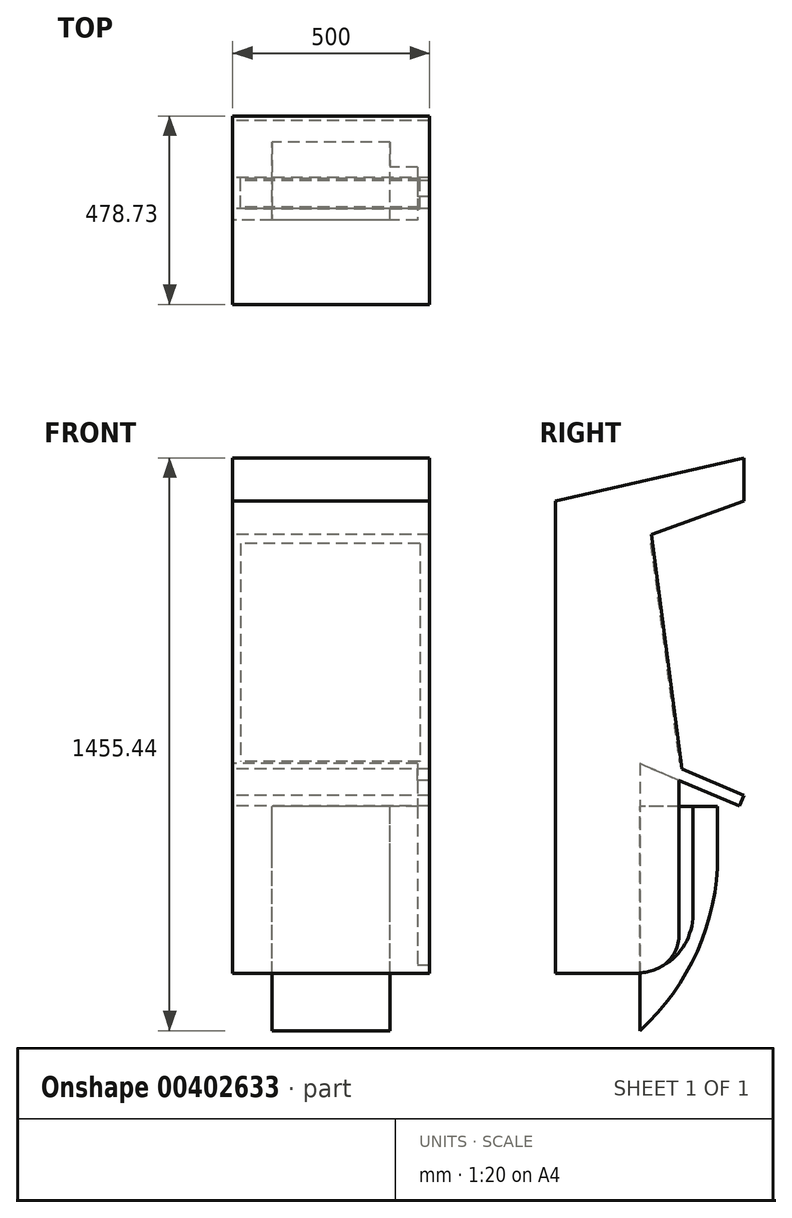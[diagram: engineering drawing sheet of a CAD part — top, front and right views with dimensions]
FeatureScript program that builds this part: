
annotation { "Feature Type Name" : "Feature", "Feature Type Description" : "" }
export const myFeature = defineFeature(function(context is Context, id is Id, definition is map)
    precondition{}
    {
        {
            var Q0;
            Q0=qCreatedBy(makeId("Right.planeOp"),FACE);
            var sketch = newSketch(context, id + "F0", { "sketchPlane" : qUnion([Q0])});
            skLineSegment(sketch, "E0", {"start": v(-1006.19, -819.62) * mm, "end": v(-1006.19, 680.38) * mm});
            skLineSegment(sketch, "E1", {"start": v(-1006.19, 680.38) * mm, "end": v(-527.46, 790.31) * mm});
            skLineSegment(sketch, "E2", {"start": v(-527.46, 790.31) * mm, "end": v(-527.46, 680.38) * mm});
            skLineSegment(sketch, "E3", {"start": v(-527.46, 680.38) * mm, "end": v(-762.41, 594.95) * mm});
            skLineSegment(sketch, "E4", {"start": v(-762.41, 594.95) * mm, "end": v(-684.7, 0) * mm});
            skLineSegment(sketch, "E5", {"start": v(-684.7, 0) * mm, "end": v(-527.46, -67.05) * mm});
            skLineSegment(sketch, "E6", {"start": v(-527.46, -67.05) * mm, "end": v(-539.23, -94.64) * mm});
            skLineSegment(sketch, "E7", {"start": v(-539.23, -94.64) * mm, "end": v(-792.2, 13.23) * mm});
            skLineSegment(sketch, "E8", {"start": v(-1006.19, -819.62) * mm, "end": v(-792.2, -819.62) * mm});
            skLineSegment(sketch, "E9", {"start": v(-792.2, 13.23) * mm, "end": v(-792.2, -819.62) * mm});
            skSolve(sketch);
        }
        {
            var Q0;
            Q0=makeQuery(id+"F0.imprint","IMPRINT",FACE,{"disambiguationData":[TD([[makeQuery(id+"F0.imprint","IMPRINT",EDGE,{"derivedFrom":sQuery(id+"F0.wireOp",EDGE,"E0")}),-1.0]])]});
            extrude(context, id + "F1", {"entities" : qUnion([Q0]), "depth" : 500 * mm});
        }
        {
            var Q0;
            Q0=makeQuery(id+"F1.opExtrude","SWEPT_FACE",FACE,{"disambiguationData":[OSD([sQuery(id+"F0.wireOp",EDGE,"E9")])]});
            var sketch = newSketch(context, id + "F2", { "sketchPlane" : qUnion([Q0])});
            skLineSegment(sketch, "E10", {"start": v(-500, -519.7) * mm, "end": v(0, -519.7) * mm});
            skLineSegment(sketch, "E11", {"start": v(0, -519.7) * mm, "end": v(0, -819.62) * mm});
            skLineSegment(sketch, "E12", {"start": v(0, -819.62) * mm, "end": v(-500, -819.62) * mm});
            skLineSegment(sketch, "E13", {"start": v(-500, -819.62) * mm, "end": v(-500, -519.7) * mm});
            skSolve(sketch);
        }
        {
            var Q0;
            Q0=makeQuery(id+"F2.imprint","IMPRINT",FACE,{"disambiguationData":[TD([[makeQuery(id+"F2.imprint","IMPRINT",EDGE,{"derivedFrom":sQuery(id+"F2.wireOp",EDGE,"E10")}),-1.0]])]});
            extrude(context, id + "F3", {"entities" : qUnion([Q0]), "operationType" : NewBodyOperationType.REMOVE, "endBound" : BoundingType.THROUGH_ALL, "oppositeDirection" : true, "depth" : 25 * mm});
        }
        {
            var Q0;
            Q0=makeQuery(id+"F1.opExtrude","SWEPT_FACE",FACE,{"disambiguationData":[OSD([sQuery(id+"F0.wireOp",EDGE,"E9")])]});
            var sketch = newSketch(context, id + "F4", { "sketchPlane" : qUnion([Q0])});
            skLineSegment(sketch, "E14.bottom", {"start": v(-500, -95.13) * mm, "end": v(-470, -95.13) * mm});
            skLineSegment(sketch, "E14.top", {"start": v(-500, -519.7) * mm, "end": v(-470, -519.7) * mm});
            skLineSegment(sketch, "E14.left", {"start": v(-500, -95.13) * mm, "end": v(-500, -519.7) * mm});
            skLineSegment(sketch, "E14.right", {"start": v(-470, -95.13) * mm, "end": v(-470, -519.7) * mm});
            skLineSegment(sketch, "E15", {"start": v(-470, -95.13) * mm, "end": v(0, -95.13) * mm});
            skLineSegment(sketch, "E16.bottom", {"start": v(0, -95.13) * mm, "end": v(-30, -95.13) * mm});
            skLineSegment(sketch, "E16.top", {"start": v(0, -519.7) * mm, "end": v(-30, -519.7) * mm});
            skLineSegment(sketch, "E16.left", {"start": v(0, -95.13) * mm, "end": v(0, -519.7) * mm});
            skLineSegment(sketch, "E16.right", {"start": v(-30, -95.13) * mm, "end": v(-30, -519.7) * mm});
            skSolve(sketch);
        }
        {
            var Q0;
            Q0=makeQuery(id+"F4.imprint","IMPRINT",FACE,{"disambiguationData":[TD([[makeQuery(id+"F4.imprint","IMPRINT",EDGE,{"derivedFrom":sQuery(id+"F4.wireOp",EDGE,"E16.bottom")}),1.0]])]});
            var Q1;
            Q1=makeQuery(id+"F4.imprint","IMPRINT",FACE,{"disambiguationData":[TD([[makeQuery(id+"F4.imprint","IMPRINT",EDGE,{"derivedFrom":sQuery(id+"F4.wireOp",EDGE,"E14.bottom")}),-1.0]])]});
            extrude(context, id + "F5", {"entities" : qUnion([Q0, Q1]), "operationType" : NewBodyOperationType.ADD, "depth" : 100 * mm});
        }
        {
            var Q0;
            Q0=makeQuery(id+"F5.opExtrude","SWEPT_FACE",FACE,{"disambiguationData":[OSD([sQuery(id+"F4.wireOp",EDGE,"E16.bottom")])]});
            var Q1;
            Q1=makeQuery(id+"F5.opExtrude","SWEPT_FACE",FACE,{"disambiguationData":[OSD([sQuery(id+"F4.wireOp",EDGE,"E14.bottom")])]});
            extrude(context, id + "F6", {"entities" : qUnion([Q0, Q1]), "operationType" : NewBodyOperationType.ADD, "depth" : 138 * mm});
        }
        {
            var Q0;
            Q0=makeQuery(id+"F5.opExtrude","CAP_EDGE",EDGE,{"disambiguationData":[OSD([sQuery(id+"F4.wireOp",EDGE,"E14.top")])],"isStart":false});
            var Q1;
            Q1=makeQuery(id+"F5.opExtrude","CAP_EDGE",EDGE,{"disambiguationData":[OSD([sQuery(id+"F4.wireOp",EDGE,"E16.top")])],"isStart":false});
            fillet(context, id + "F7", {"entities" : qUnion([Q0, Q1]), "radius" : 100 * mm, "tangentPropagation" : true, "allowEdgeOverflow" : false});
        }
        {
            var Q0;
            Q0=makeQuery(id+"F1.opExtrude","SWEPT_FACE",FACE,{"disambiguationData":[OSD([sQuery(id+"F0.wireOp",EDGE,"E9")])]});
            var sketch = newSketch(context, id + "F8", { "sketchPlane" : qUnion([Q0])});
            skLineSegment(sketch, "E17.bottom", {"start": v(-470, -519.7) * mm, "end": v(-400, -519.7) * mm});
            skLineSegment(sketch, "E17.top", {"start": v(-470, -95.55) * mm, "end": v(-400, -95.55) * mm});
            skLineSegment(sketch, "E17.left", {"start": v(-470, -519.7) * mm, "end": v(-470, -95.55) * mm});
            skLineSegment(sketch, "E17.right", {"start": v(-400, -519.7) * mm, "end": v(-400, -95.55) * mm});
            skLineSegment(sketch, "E18", {"start": v(-400, -95.55) * mm, "end": v(-30, -95.55) * mm});
            skLineSegment(sketch, "E19.bottom", {"start": v(-30, -95.55) * mm, "end": v(-100, -95.55) * mm});
            skLineSegment(sketch, "E19.top", {"start": v(-30, -519.7) * mm, "end": v(-100, -519.7) * mm});
            skLineSegment(sketch, "E19.left", {"start": v(-30, -95.55) * mm, "end": v(-30, -519.7) * mm});
            skLineSegment(sketch, "E19.right", {"start": v(-100, -95.55) * mm, "end": v(-100, -519.7) * mm});
            skSolve(sketch);
        }
        {
            var Q0;
            Q0=makeQuery(id+"F8.imprint","IMPRINT",FACE,{"disambiguationData":[TD([[makeQuery(id+"F8.imprint","IMPRINT",EDGE,{"derivedFrom":sQuery(id+"F8.wireOp",EDGE,"E17.bottom")}),1.0]])]});
            var Q1;
            Q1=makeQuery(id+"F8.imprint","IMPRINT",FACE,{"disambiguationData":[TD([[makeQuery(id+"F8.imprint","IMPRINT",EDGE,{"derivedFrom":sQuery(id+"F8.wireOp",EDGE,"E19.bottom")}),1.0]])]});
            extrude(context, id + "F9", {"entities" : qUnion([Q0, Q1]), "operationType" : NewBodyOperationType.ADD, "depth" : 135 * mm});
        }
        {
            var Q0;
            Q0=makeQuery(id+"F9.opExtrude","CAP_EDGE",EDGE,{"disambiguationData":[OSD([sQuery(id+"F8.wireOp",EDGE,"E19.top")])],"isStart":false});
            var Q1;
            Q1=makeQuery(id+"F9.opExtrude","CAP_EDGE",EDGE,{"disambiguationData":[OSD([sQuery(id+"F8.wireOp",EDGE,"E17.bottom")])],"isStart":false});
            fillet(context, id + "F10", {"entities" : qUnion([Q0, Q1]), "radius" : 149.68 * mm, "tangentPropagation" : true, "allowEdgeOverflow" : false});
        }
        {
            var Q0;
            Q0=makeQuery(id+"F1.opExtrude","SWEPT_FACE",FACE,{"disambiguationData":[OSD([sQuery(id+"F0.wireOp",EDGE,"E9")])]});
            var sketch = newSketch(context, id + "F11", { "sketchPlane" : qUnion([Q0])});
            skLineSegment(sketch, "E20", {"start": v(-400, -95.55) * mm, "end": v(-100, -95.55) * mm});
            skLineSegment(sketch, "E21", {"start": v(-400, -95.55) * mm, "end": v(-400, -665.13) * mm});
            skLineSegment(sketch, "E22", {"start": v(-400, -665.13) * mm, "end": v(-100, -665.13) * mm});
            skLineSegment(sketch, "E23", {"start": v(-100, -665.13) * mm, "end": v(-100, -95.55) * mm});
            skSolve(sketch);
        }
        {
            var Q0;
            {var subQ0=sQuery(id+"F11.wireOp",EDGE,"E20");Q0=makeQuery(id+"F11.imprint","IMPRINT",FACE,{"disambiguationData":[TD([[makeQuery(id+"F11.imprint","IMPRINT",EDGE,{"derivedFrom":subQ0}),-1.0]])]});}
            var Q1;
            {var subQ2=sQuery(id+"F11.wireOp",EDGE,"E22");Q1=makeQuery(id+"F11.imprint","IMPRINT",FACE,{"disambiguationData":[TD([[makeQuery(id+"F11.imprint","IMPRINT",EDGE,{"derivedFrom":subQ2}),1.0]])]});}
            extrude(context, id + "F12", {"entities" : qUnion([Q0, Q1]), "operationType" : NewBodyOperationType.ADD, "depth" : 198 * mm});
        }
        {
            var Q0;
            Q0=makeQuery(id+"F12.opExtrude","CAP_EDGE",EDGE,{"disambiguationData":[OSD([sQuery(id+"F11.wireOp",EDGE,"E22")])],"isStart":false});
            fillet(context, id + "F13", {"entities" : qUnion([Q0]), "radius" : 600 * mm, "tangentPropagation" : true, "allowEdgeOverflow" : false});
        }
        {
            var Q0;
            Q0=makeQuery(id+"F1.opExtrude","SWEPT_FACE",FACE,{"disambiguationData":[OSD([sQuery(id+"F0.wireOp",EDGE,"E4")])]});
            var sketch = newSketch(context, id + "F14", { "sketchPlane" : qUnion([Q0])});
            skLineSegment(sketch, "E24.bottom", {"start": v(-475.8, 666.2) * mm, "end": v(-19.8, 666.2) * mm});
            skLineSegment(sketch, "E24.top", {"start": v(-475.8, 107.8) * mm, "end": v(-19.8, 107.8) * mm});
            skLineSegment(sketch, "E24.left", {"start": v(-475.8, 666.2) * mm, "end": v(-475.8, 107.8) * mm});
            skLineSegment(sketch, "E24.right", {"start": v(-19.8, 666.2) * mm, "end": v(-19.8, 107.8) * mm});
            skSolve(sketch);
        }
        {
            var Q0;
            Q0=makeQuery(id+"F14.imprint","IMPRINT",FACE,{"disambiguationData":[TD([[makeQuery(id+"F14.imprint","IMPRINT",EDGE,{"derivedFrom":sQuery(id+"F14.wireOp",EDGE,"E24.bottom")}),-1.0]])]});
            extrude(context, id + "F15", {"entities" : qUnion([Q0]), "operationType" : NewBodyOperationType.REMOVE, "oppositeDirection" : true, "depth" : 5 * mm});
        }
    });
